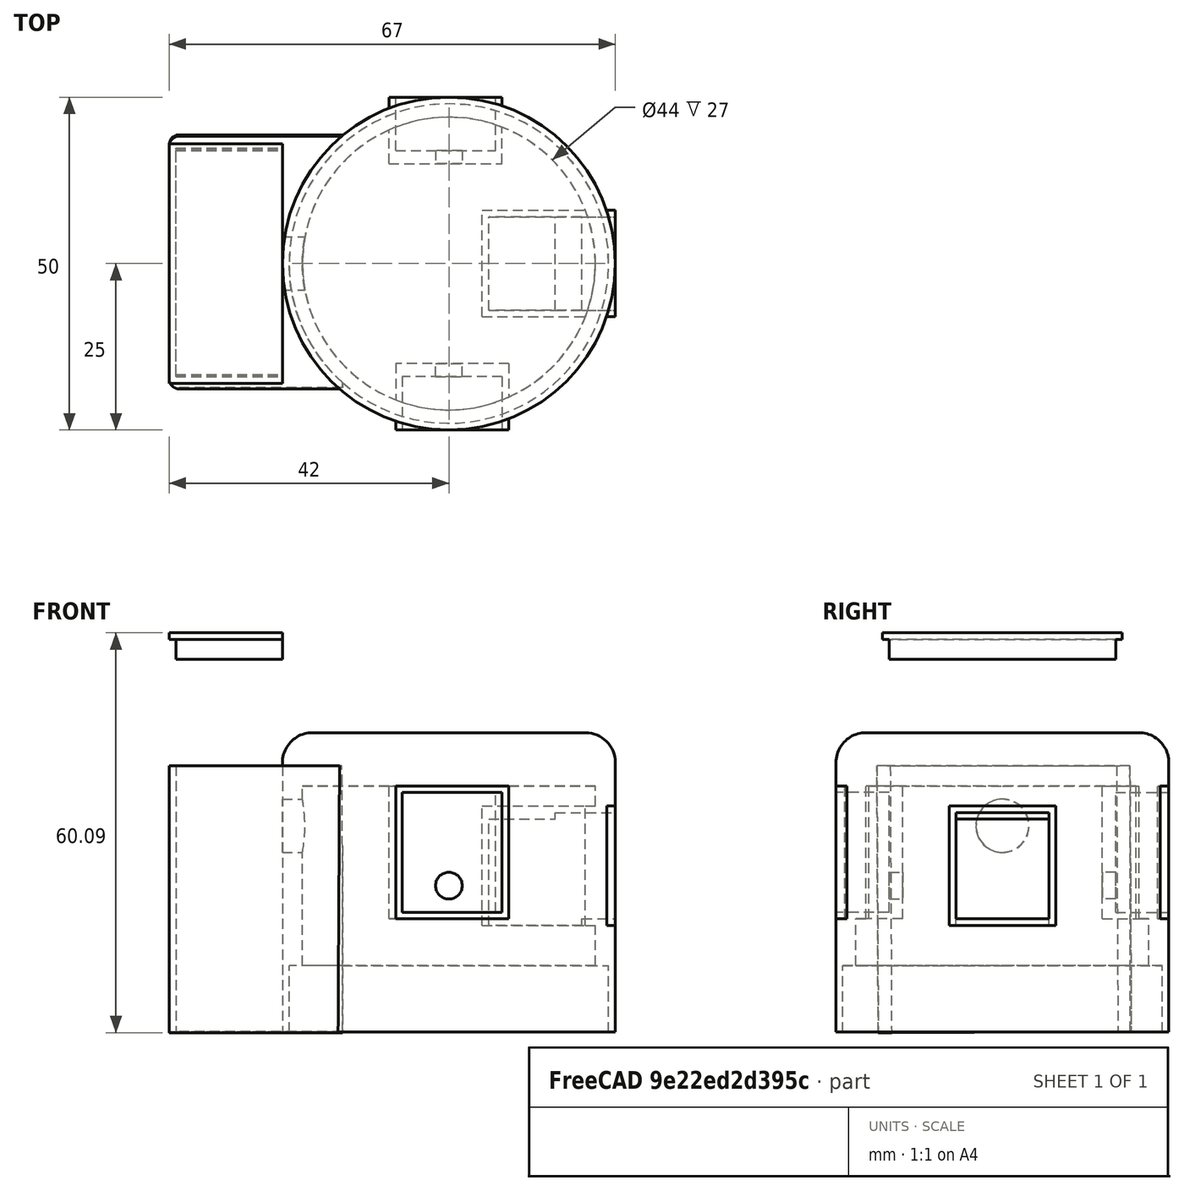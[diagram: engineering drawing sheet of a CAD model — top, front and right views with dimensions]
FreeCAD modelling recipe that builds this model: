
FCSTD DOCUMENT  (FreeCAD 0.15R4671 (Git))
Label: Lower section
License: CC-BY 3.0
LicenseURL: http://creativecommons.org/licenses/by/3.0/
objects: Part::Cut×14, Part::Box×13, Part::Cylinder×8, Part::MultiFuse×4, Part::Fillet×2
note: 41 computed .brp shape members not serialized (recipe doc carries the construction recipe); baked Part::Feature solids carry a one-line shape summary decoded from their .brp

FEATURE [Part::Cylinder] Cylinder  label="Cilindro"
  Angle = 360
  Height = 40
  Radius = 25
FEATURE [Part::Cylinder] Cylinder001  label="Cilindro001"
  Angle = 360
  Height = 37
  Radius = 22
FEATURE [Part::Cylinder] Cylinder002  label="Cilindro002"
  Angle = 360
  Height = 5
  Placement = pos=(0,0,40) rot=(0,0,1;0rad)
  Radius = 25
FEATURE [Part::Cylinder] Cylinder003  label="Cilindro003"
  Angle = 360
  Height = 10
  Radius = 24
FEATURE [Part::Fillet] Fillet
  Base = -> Cylinder002
  Edges = 1 edges r=4.5: [Edge1]
FEATURE [Part::Cut] Cut
  Base = -> Cylinder
  Tool = -> Cylinder001
FEATURE [Part::Cut] Cut001
  Base = -> Cut
  Tool = -> Cylinder003
FEATURE [Part::Box] Box  label="Cubo"
  Height = 18
  Length = 20
  Placement = pos=(5,-8,16) rot=(0,0,1;0rad)
  Width = 16
FEATURE [Part::Box] Box001  label="Cubo001"
  Height = 16
  Length = 10
  Placement = pos=(16,-7,17) rot=(0,0,1;0rad)
  Width = 14
FEATURE [Part::Box] Box002  label="Cubo002"
  Height = 20
  Length = 14
  Placement = pos=(6,-7,12) rot=(0,0,1;0rad)
  Width = 14
FEATURE [Part::Box] Box003  label="Cubo003"
  Height = 70
  Length = 16
  Placement = pos=(25,-17,1) rot=(0,0,1;0rad)
  Width = 34
FEATURE [Part::Fillet] Fillet001
  Base = -> Box001
  Edges = 5 edges r=1.5: [Edge5,Edge7,Edge8,Edge9,Edge11]
FEATURE [Part::Cut] Cut004
  Base = -> Fillet001
  Placement = pos=(0,0,70) rot=(0,0.999997,0.002488;3.14159rad)
  Tool = -> Box003
FEATURE [Part::Box] Box004  label="Cubo004"
  Height = 71
  Length = 68
  Placement = pos=(18,-8,40) rot=(0,0,1;2.26893rad)
  Width = 83
FEATURE [Part::Cut] Cut005
  Base = -> Cut004
  Tool = -> Box004
FEATURE [Part::Cylinder] Cylinder004  label="Cilindro004"
  Angle = 360
  Height = 26
  Placement = pos=(-32,0,31) rot=(0,1,0;1.5708rad)
  Radius = 4
FEATURE [Part::Box] Box005  label="Cubo005"
  Height = 20
  Length = 17
  Placement = pos=(-9,15,17) rot=(0,0,1;0rad)
  Width = 10
FEATURE [Part::MultiFuse] Fusion
  Shapes = -> [Box,Cut001]
FEATURE [Part::Cut] Cut002
  Base = -> Fusion
  Tool = -> Box001
FEATURE [Part::Cut] Cut007
  Base = -> Cut002
  Tool = -> Box002
FEATURE [Part::Cylinder] Cylinder005  label="Cilindro005"
  Angle = 360
  Height = 50
  Placement = pos=(0,0,-5) rot=(0,0,1;0rad)
  Radius = 24
FEATURE [Part::Cut] Cut008
  Base = -> Cut005
  Tool = -> Cylinder005
FEATURE [Part::MultiFuse] Fusion001
  Shapes = -> [Cut007,Cut008]
FEATURE [Part::Cut] Cut009
  Base = -> Fusion001
  Tool = -> Cylinder004
FEATURE [Part::Box] Box007  label="Cubo007"
  Height = 18
  Length = 15
  Placement = pos=(-8,17,18) rot=(0,0,1;0rad)
  Width = 8
FEATURE [Part::Cut] Cut010
  Base = -> Box005
  Tool = -> Box007
FEATURE [Part::Cylinder] Cylinder006  label="Cilindro006"
  Angle = 360
  Height = 10
  Placement = pos=(0,22,22) rot=(1,0,0;1.5708rad)
  Radius = 2
FEATURE [Part::Cut] Cut011
  Base = -> Cut010
  Tool = -> Cylinder006
FEATURE [Part::Box] Box008  label="Cubo008"
  Height = 20
  Length = 17
  Placement = pos=(-9,15,17) rot=(0,0,1;0rad)
  Width = 10
FEATURE [Part::Box] Box009  label="Cubo009"
  Height = 18
  Length = 15
  Placement = pos=(-8,17,18) rot=(0,0,1;0rad)
  Width = 8
FEATURE [Part::Cut] Cut012
  Base = -> Box008
  Tool = -> Box009
FEATURE [Part::Cylinder] Cylinder007  label="Cilindro007"
  Angle = 360
  Height = 10
  Placement = pos=(0,22,22) rot=(1,0,0;1.5708rad)
  Radius = 2
FEATURE [Part::Cut] Cut013
  Base = -> Cut012
  Placement = pos=(0,0,0) rot=(0,0,1;3.14159rad)
  Tool = -> Cylinder007
FEATURE [Part::Box] Box010  label="Cubo010"
  Height = 4
  Length = 16
  Placement = pos=(-41,-17,37) rot=(0,0,1;0rad)
  Width = 34
FEATURE [Part::Box] Box011  label="Cubo011"
  Height = 1
  Length = 17
  Placement = pos=(-42,-18,40) rot=(0,0,1;0rad)
  Width = 36
FEATURE [Part::MultiFuse] Fusion002
  Placement = pos=(0,0,19) rot=(0,0,1;0rad)
  Shapes = -> [Box010,Box011]
FEATURE [Part::Box] Box012  label="Cubo012"
  Height = 20
  Length = 17
  Placement = pos=(-9,15,17) rot=(0,0,1;0rad)
  Width = 10
FEATURE [Part::Box] Box013  label="Cubo013"
  Height = 20
  Length = 17
  Placement = pos=(9,-15,17) rot=(0,0,1;3.14159rad)
  Width = 10
FEATURE [Part::Cut] Cut014
  Base = -> Cut009
  Tool = -> Box012
FEATURE [Part::Cut] Cut015
  Base = -> Cut014
  Tool = -> Box013
FEATURE [Part::MultiFuse] Fusion003
  Shapes = -> [Fillet,Cut011,Cut013,Cut015]
